# Revit family: Drain-Floor_Adjustable_9.25_Inch_Diameter-Zurn-Z520
name_source: partatom
category: Plumbing Fixtures
units: mm (PartAtom-declared; Revit-internal decimal feet)

## family parameters
Always vertical = Yes
Cut with Voids When Loaded = No
Maintain Annotation Orientation = No
OmniClass Number = 23.70.50.21.24.14
OmniClass Title = Deck Waste Water Drains
Part Type = Normal
Room Calculation Point = No
Round Connector Dimension = Use Radius
Shared = No
Work Plane-Based = No

## types (18) — shared parameters
Assembly Code = D2030300
CW Connection = No
Default Elevation = 48 "
Description = 9-1/4 [235] DIAMETER TOP ADJUSTABLE HEAVY-DUTY DRAIN
Grate Open Area Sq.in = 15 "
HW Connection = No
Main Material = Iron - Zurn -Cast - Painted - Blue
Manufacturer = Zurn Water, LLC
Manufacurer Brand = Zurn
Modified Date = 07/23/2025
P Trap Primer Connetor = 0.25 "
Product Documentation Link = https://files.zurn.com
Product Installation Sheet = https://files.zurn.com
Product Page URL = https://www.zurn.com
Product data url = https://bimobject.com
URL = www.zurn.com
Vent Connection = No
WFU = 1
Waste Connection = Yes
Width = 12.063 "
zero-valued in all types: CWFU, HWFU

## per-type parameters (varying)
| type | Approx. Weight (Lbs) | Body Height (E) | Flange and Grate | Model | Outlet Connector Radius | Pipe Size A (Actual) | Pipe Size A (Nominal) | Top Adjustable Radius | Type Comments |
| Z520-2NH Outlet W/-P Trap | 33 " | 4.75 " | Iron - Zurn -Cast - Painted - Blue | Z520 | 1 " | 2.375 " | 2 " | 4.625 " | Z520-2 Inch -No Hub Outlet-With option for -P Trap Primer |
| Z520-2NL Outlet W/-P Trap | 33 " | 3.563 " | Iron - Zurn -Cast - Painted - Blue | Z520 | 1 " | 2.375 " | 2 " | 4.625 " | Z520-2 Inch -Neo Loc Outlet-With option for -P Trap Primer |
| Z520-3NH Outlet W/-P Trap | 33 " | 4.75 " | Iron - Zurn -Cast - Painted - Blue | Z520 | 1.5 " | 3.5 " | 3 " | 4.625 " | Z520-3 Inch -No-Hub Outlet-With option for -P Trap Primer |
| Z520-3NL Outlet W/-P Trap | 33 " | 3.563 " | Iron - Zurn -Cast - Painted - Blue | Z520 | 1.5 " | 3.5 " | 3 " | 4.625 " | Z520-3 Inch -Neo-Loc Outlet-With option for -P Trap Primer |
| Z520-4IC Outlet W/-P Trap | 33 " | 3.75 " | Iron - Zurn -Cast - Painted - Blue | Z520 | 2 " | 4.5 " | 4 " | 4.625 " | Z520-4 Inch -Inside Caulk Outlet-With option for -P Trap Primer |
| Z520-4NH Outlet W/-P Trap | 33 " | 4.75 " | Iron - Zurn -Cast - Painted - Blue | Z520 | 2 " | 4.5 " | 4 " | 4.625 " | Z520-4 Inch -No-Hub Outlet-With option for -P Trap Primer |
| Z520-4IP Outlet W/-P Trap | 33 " | 2.75 " | Iron - Zurn -Cast - Painted - Blue | Z520 | 2 " | 4.5 " | 4 " | 4.625 " | Z520-4 Inch -Threaded Outlet-With option for -P Trap Primer |
| Z520-4NL Outlet W/-P Trap | 33 " | 3.563 " | Iron - Zurn -Cast - Painted - Blue | Z520 | 2 " | 4.5 " | 4 " | 4.625 " | Z520-4 Inch -Neo-Loc Outlet-With option for -P Trap Primer |
| Z520-6NH Outlet W/-P Trap | 38 " | 5.25 " | Iron - Zurn -Cast - Painted - Blue | Z520 | 3 " | 6.625 " | 6 " | 4.625 " | Z520-6 Inch -No Hub Outlet-With option for -P Trap Primer |
| ZN520-2NH Outlet W/-P Trap | 33 " | 4.75 " | Nickel Bronze - Zurn - Polished | ZN520 | 1 " | 2.375 " | 2 " | 5.032 " | ZN520-2 Inch -No Hub Outlet-With option for -P Trap Primer |
| ZN520-2NL Outlet W/-P Trap | 33 " | 3.563 " | Nickel Bronze - Zurn - Polished | ZN520 | 1 " | 2.375 " | 2 " | 5.032 " | ZN520-2 Inch -Neo Loc Outlet-With option for -P Trap Primer |
| ZN520-3NH Outlet W/-P Trap | 33 " | 4.75 " | Nickel Bronze - Zurn - Polished | ZN520 | 1.5 " | 3.5 " | 3 " | 5.032 " | ZN520-3 Inch -No-Hub Outlet-With option for -P Trap Primer |
| ZN520-3NL Outlet W/-P Trap | 33 " | 3.563 " | Nickel Bronze - Zurn - Polished | ZN520 | 1.5 " | 3.5 " | 3 " | 5.032 " | ZN520-3 Inch -Neo-Loc Outlet-With option for -P Trap Primer |
| ZN520-4IC Outlet W/-P Trap | 33 " | 3.75 " | Nickel Bronze - Zurn - Polished | ZN520 | 2 " | 4.5 " | 4 " | 5.032 " | ZN520-4 Inch -Inside Caulk Outlet-With option for -P Trap Primer |
| ZN520-4NH Outlet W/-P Trap | 33 " | 4.75 " | Nickel Bronze - Zurn - Polished | ZN520 | 2 " | 4.5 " | 4 " | 5.032 " | ZN520-4 Inch -No-Hub Outlet-With option for -P Trap Primer |
| ZN520-4IP Outlet W/-P Trap | 33 " | 2.75 " | Nickel Bronze - Zurn - Polished | ZN520 | 2 " | 4.5 " | 4 " | 5.032 " | ZN520-4 Inch -Threaded Outlet-With option for -P Trap Primer |
| ZN520-4NL Outlet W/-P Trap | 33 " | 3.563 " | Nickel Bronze - Zurn - Polished | ZN520 | 2 " | 4.5 " | 4 " | 5.032 " | ZN520-4 Inch -Neo-Loc Outlet-With option for -P Trap Primer |
| ZN520-6NH Outlet W/-P Trap | 38 " | 5.25 " | Nickel Bronze - Zurn - Polished | ZN520 | 3 " | 6.625 " | 6 " | 5.032 " | ZN520-6 Inch -No Hub Outlet-With option for -P Trap Primer |

## geometry (parser evidence)
native form markers: Sweep x4
no freeform markers — native parametric forms only
